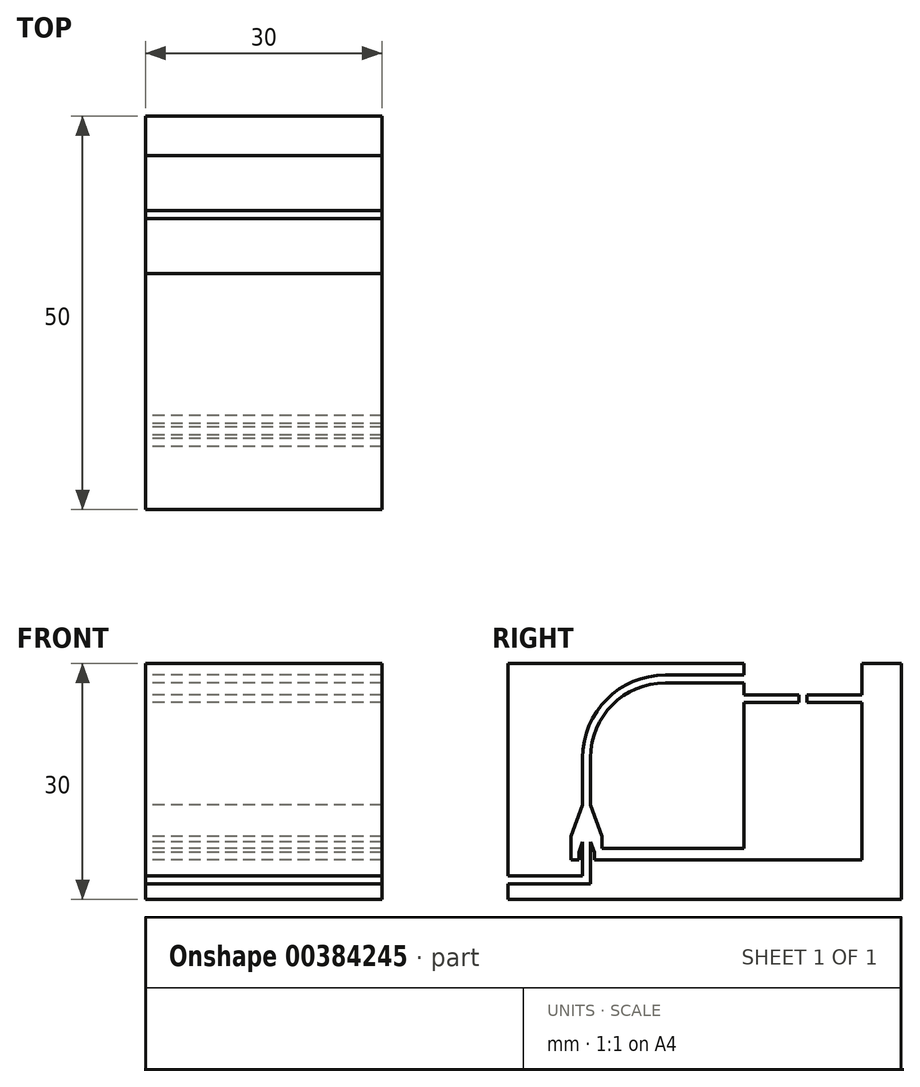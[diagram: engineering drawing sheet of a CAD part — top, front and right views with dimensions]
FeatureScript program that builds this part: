
annotation { "Feature Type Name" : "Feature", "Feature Type Description" : "" }
export const myFeature = defineFeature(function(context is Context, id is Id, definition is map)
    precondition{}
    {
        {
            var Q0;
            Q0=qCreatedBy(makeId("Right.planeOp"),FACE);
            var sketch = newSketch(context, id + "F0", { "sketchPlane" : qUnion([Q0])});
            skLineSegment(sketch, "E0.bottom", {"start": v(0, 0) * mm, "end": v(50, 0) * mm});
            skLineSegment(sketch, "E0.top", {"start": v(0, 30) * mm, "end": v(30, 30) * mm});
            skLineSegment(sketch, "E0.left", {"start": v(0, 0) * mm, "end": v(0, 2) * mm});
            skLineSegment(sketch, "E0.right", {"start": v(50, 0) * mm, "end": v(50, 30) * mm});
            skLineSegment(sketch, "E1.top", {"start": v(45, 5) * mm, "end": v(30, 5) * mm});
            skLineSegment(sketch, "E1.left", {"start": v(45, 30) * mm, "end": v(45, 26) * mm});
            skLineSegment(sketch, "E1.right", {"start": v(30, 30) * mm, "end": v(30, 28.5) * mm});
            skLineSegment(sketch, "E2", {"start": v(10, 25.1) * mm, "end": v(10, 18) * mm, "construction": true});
            skLineSegment(sketch, "E3", {"start": v(20, 28) * mm, "end": v(30, 28) * mm, "construction": true});
            skPoint(sketch, "E4.visualSharp", {"position": v(10, 28) * mm});
            skArc(sketch, "E4.filletArc", {"start": v(20, 28) * mm, "mid": v(12.93, 25.07) * mm, "end": v(10, 18) * mm, "construction": true});
            skLineSegment(sketch, "E5.0", {"start": v(9.5, 18) * mm, "end": v(9.5, 12) * mm});
            skArc(sketch, "E5.1", {"start": v(20, 28.5) * mm, "mid": v(12.58, 25.42) * mm, "end": v(9.5, 18) * mm});
            skLineSegment(sketch, "E5.2", {"start": v(20, 28.5) * mm, "end": v(30, 28.5) * mm});
            skLineSegment(sketch, "E6", {"start": v(9.5, 12) * mm, "end": v(8.04, 8) * mm});
            skLineSegment(sketch, "E7", {"start": v(8.04, 8) * mm, "end": v(8.04, 5) * mm});
            skLineSegment(sketch, "E8", {"start": v(8.04, 5) * mm, "end": v(9.02, 5) * mm});
            skLineSegment(sketch, "E9.MirrorCS", {"start": v(10.5, 12) * mm, "end": v(11.96, 8) * mm});
            skLineSegment(sketch, "E10.MirrorCS", {"start": v(11.96, 8) * mm, "end": v(11.96, 6.5) * mm});
            skLineSegment(sketch, "E11.MirrorCS", {"start": v(11.96, 5) * mm, "end": v(10.98, 5) * mm});
            skLineSegment(sketch, "E12.MirrorCS", {"start": v(10.5, 18) * mm, "end": v(10.5, 12) * mm});
            skLineSegment(sketch, "E13", {"start": v(11.96, 5) * mm, "end": v(30, 5) * mm});
            skLineSegment(sketch, "E14", {"start": v(11.96, 6.5) * mm, "end": v(30, 6.5) * mm});
            skLineSegment(sketch, "E15.trimOffspring", {"start": v(30, 30) * mm, "end": v(30, 26) * mm});
            skLineSegment(sketch, "E16.trimOffspring", {"start": v(45, 30) * mm, "end": v(50, 30) * mm});
            skLineSegment(sketch, "E17", {"start": v(9.02, 5) * mm, "end": v(9.02, 6) * mm});
            skLineSegment(sketch, "E18", {"start": v(9.02, 6) * mm, "end": v(9.5, 7.31) * mm});
            skLineSegment(sketch, "E19", {"start": v(9.5, 7.31) * mm, "end": v(9.5, 5) * mm});
            skLineSegment(sketch, "E20.MirrorCS", {"start": v(10.98, 5) * mm, "end": v(10.98, 6) * mm});
            skLineSegment(sketch, "E21.MirrorCS", {"start": v(10.98, 6) * mm, "end": v(10.5, 7.31) * mm});
            skLineSegment(sketch, "E22.MirrorCS", {"start": v(10.5, 7.31) * mm, "end": v(10.5, 5) * mm});
            skLineSegment(sketch, "E23", {"start": v(9.5, 5) * mm, "end": v(9.5, 3) * mm});
            skLineSegment(sketch, "E24", {"start": v(9.5, 3) * mm, "end": v(0, 3) * mm});
            skLineSegment(sketch, "E25", {"start": v(10.5, 5) * mm, "end": v(10.5, 2) * mm});
            skLineSegment(sketch, "E26", {"start": v(10.5, 2) * mm, "end": v(0, 2) * mm});
            skLineSegment(sketch, "E27.trimOffspring", {"start": v(0, 3) * mm, "end": v(0, 30) * mm});
            skPoint(sketch, "E28.trimOffspring.end.orphan", {"position": v(10, 5) * mm});
            skLineSegment(sketch, "E29.0", {"start": v(20, 27.5) * mm, "end": v(30, 27.5) * mm});
            skArc(sketch, "E29.1", {"start": v(20, 27.5) * mm, "mid": v(13.28, 24.72) * mm, "end": v(10.5, 18) * mm});
            skLineSegment(sketch, "E30.bottom", {"start": v(30, 26) * mm, "end": v(37, 26) * mm});
            skLineSegment(sketch, "E30.top", {"start": v(30, 25) * mm, "end": v(37, 25) * mm});
            skLineSegment(sketch, "E31.left", {"start": v(38, 26) * mm, "end": v(38, 25) * mm});
            skLineSegment(sketch, "E31.right", {"start": v(37, 26) * mm, "end": v(37, 25) * mm});
            skPoint(sketch, "E31.middle", {"position": v(37.5, 25) * mm});
            skLineSegment(sketch, "E32.trimOffspring", {"start": v(38, 26) * mm, "end": v(45, 26) * mm});
            skLineSegment(sketch, "E33.trimOffspring", {"start": v(38, 25) * mm, "end": v(45, 25) * mm});
            skLineSegment(sketch, "E34", {"start": v(37.5, 25) * mm, "end": v(37.5, 26) * mm, "construction": true});
            skLineSegment(sketch, "E35.trimOffspring", {"start": v(30, 25) * mm, "end": v(30, 6.5) * mm});
            skLineSegment(sketch, "E36.trimOffspring", {"start": v(45, 25) * mm, "end": v(45, 5) * mm});
            skSolve(sketch);
        }
        {
            var Q0;
            Q0 = qSketchRegion(id + "F0", true);
            extrude(context, id + "F1", {"entities" : qUnion([Q0]), "endBound" : BoundingType.SYMMETRIC, "depth" : 30 * mm});
        }
    });
